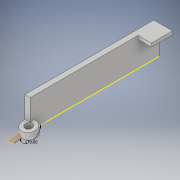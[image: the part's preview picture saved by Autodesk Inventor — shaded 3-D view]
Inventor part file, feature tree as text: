
AUTODESK INVENTOR PART (.ipt)
format: ipt  version: 2017 (Build 210142000, 142)  size: 162,816 bytes
history: native  units: in
note: dims shown in document units (in); Inventor stores cm internally (conversion verified against a paired STEP export)
features: sketch x6, extrude x5, projected_geometry x5, plane x1
ambient origin geometry x8: Origin, YZ Plane, XZ Plane, XY Plane, X Axis, Y Axis, Z Axis, Center Point
bodies: Body1 (feature_tree)
feature tree (17):
  extrude  "Extrusion2"  Depth=4.5in
  sketch  "Sketch3"  dims[d8=0.1875in d9=0.0in d10=1.1681in]
  plane  "Work Plane1"
  sketch  "Sketch4"  dims[d18=0.125in d19=0.0in d28=0.5in]
  extrude  "Extrusion4"  Depth=0.1875in
  extrude  "Extrusion6"  Depth=0.125in
  extrude  "Extrusion8"  Depth=0.1875in
  extrude  "Extrusion9"  Depth=0.25in
  sketch  "Sketch2"  dims[d6=1.0in d7=4.5in]
  projected_geometry  "Projected Loop1"
  sketch  "Sketch5"  dims[d29=0.1875in d30=0.0625in]
  projected_geometry  "Projected Loop2"
  sketch  "Sketch9"  dims[d32=0.25in d33=0.0in d36=0.25in]
  projected_geometry  "Projected Loop7"
  sketch  "Sketch10"  dims[d37=0.5in d38=0.0in d40=0.075in d41=0.4846in d42=0.2423in d43=0.6871in d44=0.35in d45=0.1in d46=0.0in]
  projected_geometry  "Projected Loop8"
  projected_geometry  "Projected Loop9"
